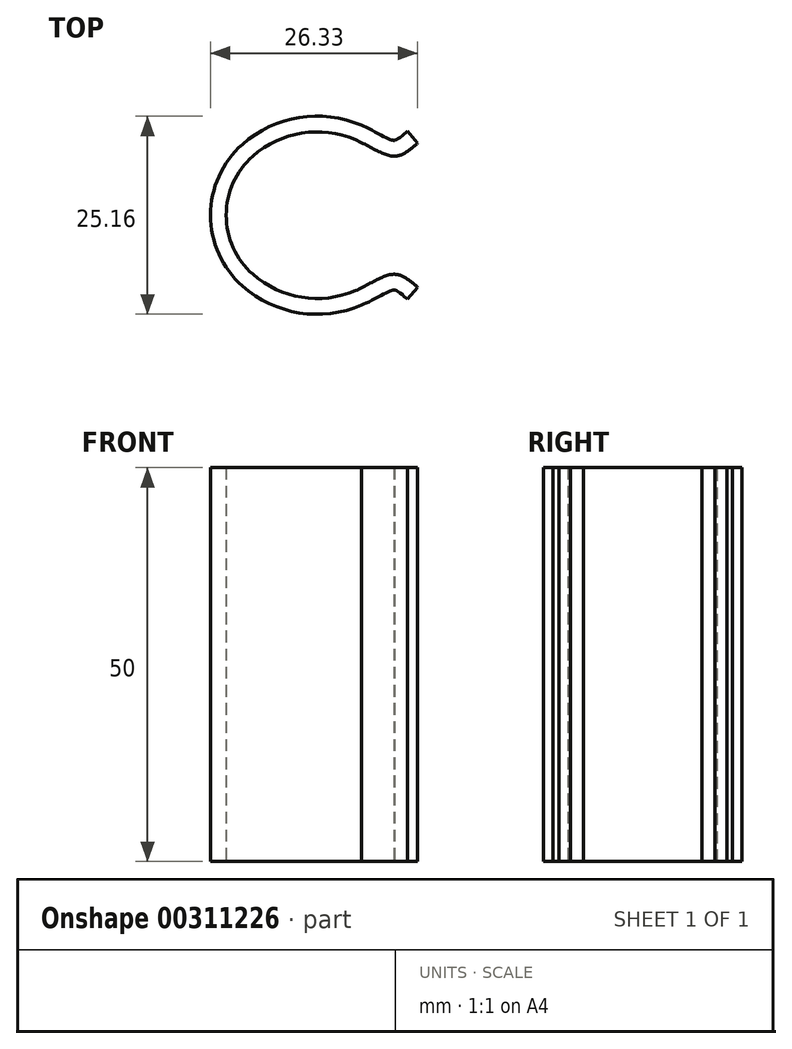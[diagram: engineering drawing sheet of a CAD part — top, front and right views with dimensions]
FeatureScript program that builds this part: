
annotation { "Feature Type Name" : "Feature", "Feature Type Description" : "" }
export const myFeature = defineFeature(function(context is Context, id is Id, definition is map)
    precondition{}
    {
        {
            var Q0;
            Q0=qCreatedBy(makeId("Top.planeOp"),FACE);
            var sketch = newSketch(context, id + "F0", { "sketchPlane" : qUnion([Q0])});
            skLineSegment(sketch, "E0.bottom", {"start": v(0, 0) * mm, "end": v(18, 0) * mm});
            skLineSegment(sketch, "E0.top", {"start": v(0, 15) * mm, "end": v(18, 15) * mm});
            skLineSegment(sketch, "E0.left", {"start": v(0, 0) * mm, "end": v(0, 15) * mm});
            skLineSegment(sketch, "E0.right", {"start": v(18, 0) * mm, "end": v(18, 15) * mm});
            skLineSegment(sketch, "E1", {"start": v(-14.98, 7.5) * mm, "end": v(45.19, 7.5) * mm, "construction": true});
            skPoint(sketch, "E1.startSnap0", {"position": v(0, 7.5) * mm});
            skArc(sketch, "E2", {"start": v(0, 15) * mm, "mid": v(-3.39, 7.5) * mm, "end": v(0, 0) * mm});
            skArc(sketch, "E3", {"start": v(0, 15) * mm, "mid": v(6.2, 17.93) * mm, "end": v(13.01, 17.09) * mm});
            skFitSpline(sketch, "E4", {"points": [v(13.01, 17.09) * mm, v(18, 15) * mm, v(20.94, 16.67) * mm], "startDerivative": vector(10.47, -4.49) * mm, "endDerivative": vector(6.17, 5.48) * mm});
            skArc(sketch, "E5.MirrorCS", {"start": v(0, 0) * mm, "mid": v(6.2, -2.93) * mm, "end": v(13.01, -2.09) * mm});
            skFitSpline(sketch, "E6.MirrorCS", {"points": [v(13.01, -2.09) * mm, v(18, 0) * mm, v(20.94, -1.67) * mm], "startDerivative": vector(10.47, 4.49) * mm, "endDerivative": vector(6.17, -5.48) * mm});
            skFitSpline(sketch, "E7.0", {"points": [v(13.8, 18.92) * mm, v(14.3, 18.7) * mm, v(15.24, 18.24) * mm, v(16.22, 17.7) * mm, v(16.9, 17.36) * mm, v(17.32, 17.17) * mm, v(17.6, 17.07) * mm, v(17.77, 17.02) * mm, v(17.87, 17) * mm, v(17.93, 17) * mm, v(17.96, 17) * mm, v(17.98, 17) * mm, v(18.03, 17) * mm, v(18.13, 17.04) * mm, v(18.4, 17.17) * mm, v(18.87, 17.51) * mm, v(19.35, 17.94) * mm, v(19.61, 18.17) * mm]});
            skFitSpline(sketch, "E7.1", {"points": [v(13.8, -3.92) * mm, v(14.3, -3.7) * mm, v(15.24, -3.24) * mm, v(16.22, -2.7) * mm, v(16.9, -2.36) * mm, v(17.32, -2.17) * mm, v(17.6, -2.07) * mm, v(17.77, -2.02) * mm, v(17.87, -2) * mm, v(17.93, -2) * mm, v(17.96, -2) * mm, v(17.98, -2) * mm, v(18.03, -2) * mm, v(18.13, -2.04) * mm, v(18.4, -2.17) * mm, v(18.87, -2.51) * mm, v(19.35, -2.94) * mm, v(19.61, -3.17) * mm]});
            skArc(sketch, "E7.2", {"start": v(-1.32, -1.5) * mm, "mid": v(5.89, -4.9) * mm, "end": v(13.8, -3.92) * mm});
            skArc(sketch, "E7.3", {"start": v(-1.32, 16.5) * mm, "mid": v(-5.39, 7.5) * mm, "end": v(-1.32, -1.5) * mm});
            skArc(sketch, "E7.4", {"start": v(-1.32, 16.5) * mm, "mid": v(5.89, 19.9) * mm, "end": v(13.8, 18.92) * mm});
            skLineSegment(sketch, "E8", {"start": v(19.61, 18.17) * mm, "end": v(20.94, 16.67) * mm});
            skLineSegment(sketch, "E9", {"start": v(20.94, -1.67) * mm, "end": v(19.61, -3.17) * mm});
            skSolve(sketch);
        }
        {
            var Q0;
            Q0=makeQuery(id+"F0.imprint","IMPRINT",FACE,{"disambiguationData":[TD([[makeQuery(id+"F0.imprint","IMPRINT",EDGE,{"derivedFrom":sQuery(id+"F0.wireOp",EDGE,"E2")}),-1.0]])]});
            extrude(context, id + "F1", {"entities" : qUnion([Q0]), "depth" : 50 * mm, "offsetDistance" : 25 * mm});
        }
    });
